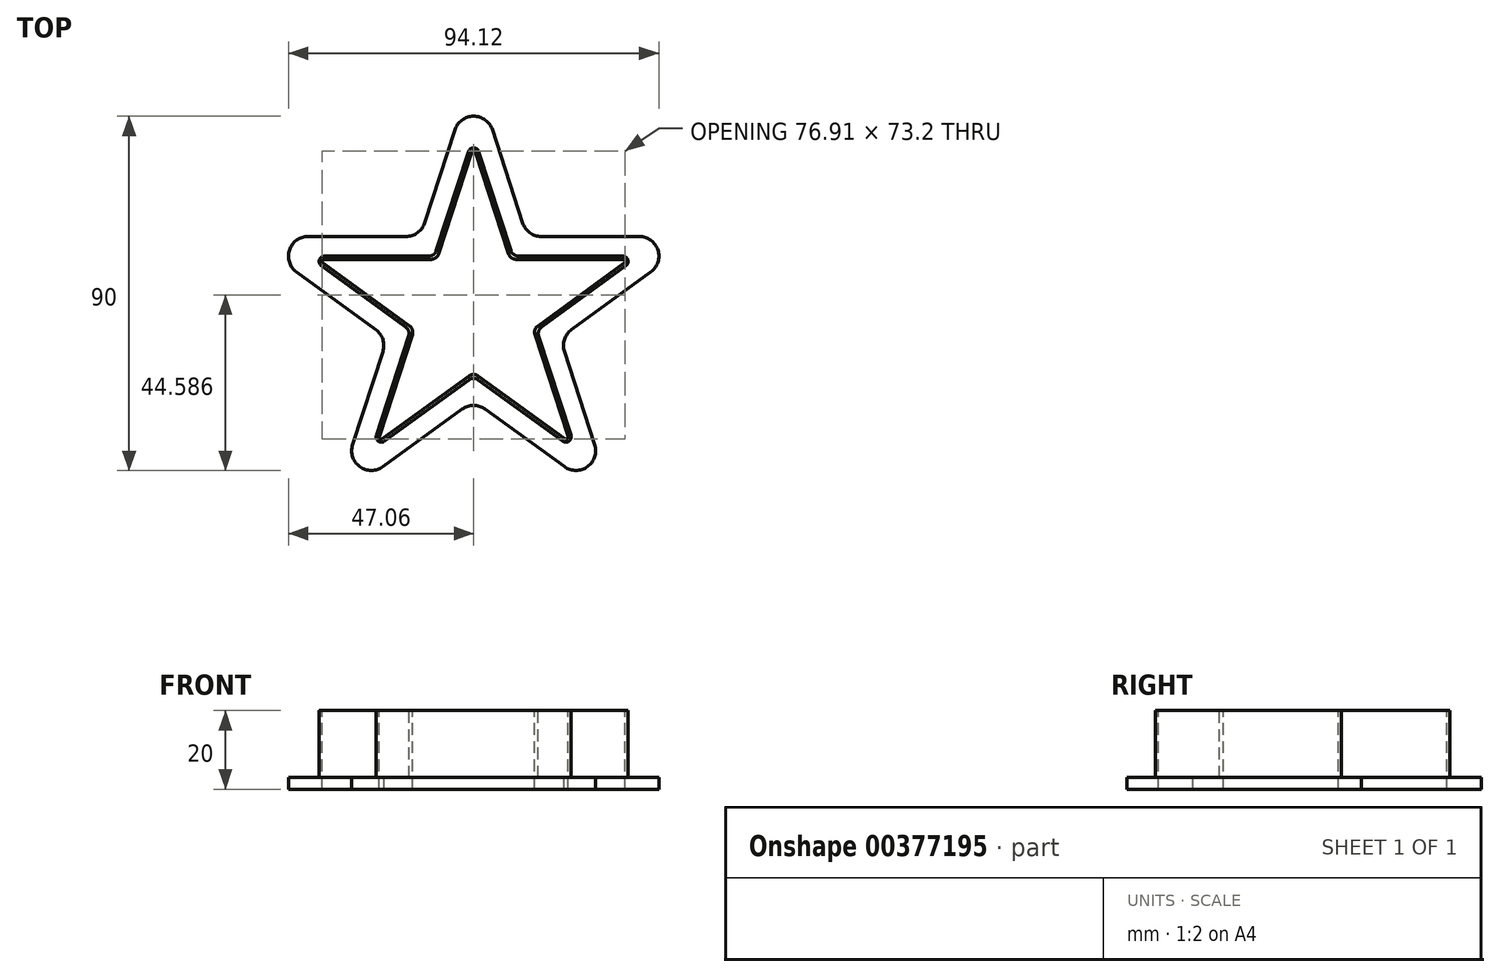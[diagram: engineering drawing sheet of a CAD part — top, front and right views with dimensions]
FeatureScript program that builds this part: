
annotation { "Feature Type Name" : "Feature", "Feature Type Description" : "" }
export const myFeature = defineFeature(function(context is Context, id is Id, definition is map)
    precondition{}
    {
        {
            var Q0;
            Q0=qCreatedBy(makeId("Top.planeOp"),FACE);
            var sketch = newSketch(context, id + "F0", { "sketchPlane" : qUnion([Q0])});
            skPoint(sketch, "E0.0.midPoint", {"position": v(8.03, -32.44) * mm});
            skPoint(sketch, "E1.endSnap0", {"position": v(0, -7.72) * mm});
            skLineSegment(sketch, "E2", {"start": v(-9.93, 13.67) * mm, "end": v(-1.28, 40.27) * mm});
            skLineSegment(sketch, "E3", {"start": v(1.28, 40.27) * mm, "end": v(9.93, 13.67) * mm});
            skLineSegment(sketch, "E4.1.0", {"start": v(-16.06, -5.22) * mm, "end": v(-38.7, 11.22) * mm});
            skLineSegment(sketch, "E4.1.1", {"start": v(-37.9, 13.67) * mm, "end": v(-9.93, 13.67) * mm});
            skLineSegment(sketch, "E4.2.0", {"start": v(0, -16.9) * mm, "end": v(-22.63, -33.33) * mm});
            skLineSegment(sketch, "E4.2.1", {"start": v(-24.7, -31.83) * mm, "end": v(-16.06, -5.22) * mm});
            skLineSegment(sketch, "E4.3.0", {"start": v(16.06, -5.22) * mm, "end": v(24.7, -31.83) * mm});
            skLineSegment(sketch, "E4.3.1", {"start": v(22.63, -33.33) * mm, "end": v(0, -16.9) * mm});
            skLineSegment(sketch, "E4.4.0", {"start": v(9.93, 13.67) * mm, "end": v(37.9, 13.67) * mm});
            skLineSegment(sketch, "E4.4.1", {"start": v(38.7, 11.22) * mm, "end": v(16.06, -5.22) * mm});
            skPoint(sketch, "E4.center", {"position": v(0, 0) * mm});
            skLineSegment(sketch, "E5.0", {"start": v(-57.45, 18.67) * mm, "end": v(-13.56, 18.67) * mm});
            skLineSegment(sketch, "E5.1", {"start": v(-21.94, -7.13) * mm, "end": v(-57.45, 18.67) * mm});
            skLineSegment(sketch, "E5.2", {"start": v(-13.56, 18.67) * mm, "end": v(0, 60.4) * mm});
            skLineSegment(sketch, "E5.3", {"start": v(-35.5, -48.87) * mm, "end": v(-21.94, -7.13) * mm});
            skLineSegment(sketch, "E5.4", {"start": v(0, -23.07) * mm, "end": v(-35.5, -48.87) * mm});
            skLineSegment(sketch, "E5.5", {"start": v(35.5, -48.87) * mm, "end": v(0, -23.07) * mm});
            skLineSegment(sketch, "E5.6", {"start": v(0, 60.4) * mm, "end": v(13.56, 18.67) * mm});
            skLineSegment(sketch, "E5.7", {"start": v(13.56, 18.67) * mm, "end": v(57.45, 18.67) * mm});
            skLineSegment(sketch, "E5.8", {"start": v(57.45, 18.67) * mm, "end": v(21.94, -7.13) * mm});
            skLineSegment(sketch, "E5.9", {"start": v(21.94, -7.13) * mm, "end": v(35.5, -48.87) * mm});
            skLineSegment(sketch, "E6.0", {"start": v(-15.12, -4.91) * mm, "end": v(-38.23, 11.87) * mm});
            skLineSegment(sketch, "E6.1", {"start": v(-23.95, -32.07) * mm, "end": v(-15.12, -4.91) * mm});
            skLineSegment(sketch, "E6.2", {"start": v(-37.9, 12.87) * mm, "end": v(-9.35, 12.87) * mm});
            skLineSegment(sketch, "E6.3", {"start": v(0, -15.9) * mm, "end": v(-23.1, -32.69) * mm});
            skLineSegment(sketch, "E6.4", {"start": v(23.1, -32.69) * mm, "end": v(0, -15.9) * mm});
            skLineSegment(sketch, "E6.5", {"start": v(15.12, -4.91) * mm, "end": v(23.95, -32.07) * mm});
            skLineSegment(sketch, "E6.6", {"start": v(-9.35, 12.87) * mm, "end": v(-0.52, 40.02) * mm});
            skLineSegment(sketch, "E6.7", {"start": v(0.52, 40.02) * mm, "end": v(9.35, 12.87) * mm});
            skLineSegment(sketch, "E6.8", {"start": v(9.35, 12.87) * mm, "end": v(37.9, 12.87) * mm});
            skLineSegment(sketch, "E6.9", {"start": v(38.23, 11.87) * mm, "end": v(15.12, -4.91) * mm});
            skPoint(sketch, "E7.visualSharp", {"position": v(39.6, 12.87) * mm});
            skArc(sketch, "E7.filletArc", {"start": v(38.23, 11.87) * mm, "mid": v(38.43, 12.49) * mm, "end": v(37.9, 12.87) * mm});
            skPoint(sketch, "E8.visualSharp", {"position": v(42.06, 13.67) * mm});
            skArc(sketch, "E8.filletArc", {"start": v(38.7, 11.22) * mm, "mid": v(39.19, 12.73) * mm, "end": v(37.9, 13.67) * mm});
            skPoint(sketch, "E9.visualSharp", {"position": v(0, 41.63) * mm});
            skArc(sketch, "E9.filletArc", {"start": v(0.52, 40.02) * mm, "mid": v(0, 40.4) * mm, "end": v(-0.52, 40.02) * mm});
            skPoint(sketch, "E10.visualSharp", {"position": v(-39.6, 12.87) * mm});
            skArc(sketch, "E10.filletArc", {"start": v(-37.9, 12.87) * mm, "mid": v(-38.43, 12.49) * mm, "end": v(-38.23, 11.87) * mm});
            skPoint(sketch, "E11.visualSharp", {"position": v(-24.47, -33.68) * mm});
            skArc(sketch, "E11.filletArc", {"start": v(-23.95, -32.07) * mm, "mid": v(-23.75, -32.69) * mm, "end": v(-23.1, -32.69) * mm});
            skPoint(sketch, "E12.visualSharp", {"position": v(24.47, -33.68) * mm});
            skArc(sketch, "E12.filletArc", {"start": v(23.1, -32.69) * mm, "mid": v(23.75, -32.69) * mm, "end": v(23.95, -32.07) * mm});
            skPoint(sketch, "E13.visualSharp", {"position": v(0, 44.22) * mm});
            skArc(sketch, "E13.filletArc", {"start": v(1.28, 40.27) * mm, "mid": v(0, 41.2) * mm, "end": v(-1.28, 40.27) * mm});
            skPoint(sketch, "E14.visualSharp", {"position": v(-42.06, 13.67) * mm});
            skArc(sketch, "E14.filletArc", {"start": v(-37.9, 13.67) * mm, "mid": v(-39.19, 12.73) * mm, "end": v(-38.7, 11.22) * mm});
            skPoint(sketch, "E15.visualSharp", {"position": v(-26, -35.78) * mm});
            skArc(sketch, "E15.filletArc", {"start": v(-24.7, -31.83) * mm, "mid": v(-24.22, -33.33) * mm, "end": v(-22.63, -33.33) * mm});
            skPoint(sketch, "E16.visualSharp", {"position": v(26, -35.78) * mm});
            skArc(sketch, "E16.filletArc", {"start": v(22.63, -33.33) * mm, "mid": v(24.22, -33.33) * mm, "end": v(24.7, -31.83) * mm});
            skSolve(sketch);
        }
        {
            var Q0;
            Q0=makeQuery(id+"F0.imprint","IMPRINT",FACE,{"disambiguationData":[TD([[makeQuery(id+"F0.imprint","IMPRINT",EDGE,{"derivedFrom":sQuery(id+"F0.wireOp",EDGE,"E2")}),1.0]])]});
            var Q1;
            Q1=makeQuery(id+"F0.imprint","IMPRINT",FACE,{"disambiguationData":[TD([[makeQuery(id+"F0.imprint","IMPRINT",EDGE,{"derivedFrom":sQuery(id+"F0.wireOp",EDGE,"E2")}),-1.0]])]});
            extrude(context, id + "F1", {"entities" : qUnion([Q0, Q1]), "oppositeDirection" : true, "depth" : 3 * mm});
        }
        {
            var Q0;
            Q0=makeQuery(id+"F0.imprint","IMPRINT",FACE,{"disambiguationData":[TD([[makeQuery(id+"F0.imprint","IMPRINT",EDGE,{"derivedFrom":sQuery(id+"F0.wireOp",EDGE,"E2")}),-1.0]])]});
            extrude(context, id + "F2", {"entities" : qUnion([Q0]), "operationType" : NewBodyOperationType.ADD, "depth" : 17 * mm});
        }
        {
            var Q0;
            Q0=makeQuery(id+"F1.opExtrude","SWEPT_EDGE",EDGE,{"disambiguationData":[OSD([sQuery(id+"F0.wireOp",EDGE,"E5.3"),sQuery(id+"F0.wireOp",EDGE,"E5.4")])]});
            var Q1;
            Q1=makeQuery(id+"F1.opExtrude","SWEPT_EDGE",EDGE,{"disambiguationData":[OSD([sQuery(id+"F0.wireOp",EDGE,"E5.0"),sQuery(id+"F0.wireOp",EDGE,"E5.1")])]});
            var Q2;
            Q2=makeQuery(id+"F1.opExtrude","SWEPT_EDGE",EDGE,{"disambiguationData":[OSD([sQuery(id+"F0.wireOp",EDGE,"E5.5"),sQuery(id+"F0.wireOp",EDGE,"E5.9")])]});
            var Q3;
            Q3=makeQuery(id+"F1.opExtrude","SWEPT_EDGE",EDGE,{"disambiguationData":[OSD([sQuery(id+"F0.wireOp",EDGE,"E5.2"),sQuery(id+"F0.wireOp",EDGE,"E5.6")])]});
            var Q4;
            Q4=makeQuery(id+"F1.opExtrude","SWEPT_EDGE",EDGE,{"disambiguationData":[OSD([sQuery(id+"F0.wireOp",EDGE,"E5.7"),sQuery(id+"F0.wireOp",EDGE,"E5.8")])]});
            fillet(context, id + "F3", {"entities" : qUnion([Q0, Q1, Q2, Q3, Q4]), "radius" : 5 * mm, "tangentPropagation" : true, "allowEdgeOverflow" : false});
        }
        {
            var Q0;
            Q0=makeQuery(id+"F1.opExtrude","SWEPT_EDGE",EDGE,{"disambiguationData":[OSD([sQuery(id+"F0.wireOp",EDGE,"E5.1"),sQuery(id+"F0.wireOp",EDGE,"E5.3")])]});
            var Q1;
            Q1=makeQuery(id+"F1.opExtrude","SWEPT_EDGE",EDGE,{"disambiguationData":[OSD([sQuery(id+"F0.wireOp",EDGE,"E5.0"),sQuery(id+"F0.wireOp",EDGE,"E5.2")])]});
            var Q2;
            Q2=makeQuery(id+"F1.opExtrude","SWEPT_EDGE",EDGE,{"disambiguationData":[OSD([sQuery(id+"F0.wireOp",EDGE,"E5.6"),sQuery(id+"F0.wireOp",EDGE,"E5.7")])]});
            var Q3;
            Q3=makeQuery(id+"F1.opExtrude","SWEPT_EDGE",EDGE,{"disambiguationData":[OSD([sQuery(id+"F0.wireOp",EDGE,"E5.8"),sQuery(id+"F0.wireOp",EDGE,"E5.9")])]});
            var Q4;
            Q4=makeQuery(id+"F1.opExtrude","SWEPT_EDGE",EDGE,{"disambiguationData":[OSD([sQuery(id+"F0.wireOp",EDGE,"E5.4"),sQuery(id+"F0.wireOp",EDGE,"E5.5")])]});
            fillet(context, id + "F4", {"entities" : qUnion([Q0, Q1, Q2, Q3, Q4]), "radius" : 5 * mm, "tangentPropagation" : true, "allowEdgeOverflow" : false});
        }
        {
            var Q0;
            {var subQ0=sQuery(id+"F0.wireOp",EDGE,"E6.6");var subQ1=sQuery(id+"F0.wireOp",EDGE,"E6.2");Q0=makeQuery(id+"F2.boolean.opBoolean","MERGE",EDGE,{"derivedFrom":[makeQuery(id+"F1.opExtrude","SWEPT_EDGE",EDGE,{"disambiguationData":[OSD([subQ1,subQ0])]}),makeQuery(id+"F2.opExtrude","SWEPT_EDGE",EDGE,{"disambiguationData":[OSD([subQ1,subQ0])]})]});}
            var Q1;
            Q1=makeQuery(id+"F2.opExtrude","SWEPT_EDGE",EDGE,{"disambiguationData":[OSD([sQuery(id+"F0.wireOp",EDGE,"E2"),sQuery(id+"F0.wireOp",EDGE,"E4.1.1")])]});
            var Q2;
            Q2=makeQuery(id+"F2.opExtrude","SWEPT_EDGE",EDGE,{"disambiguationData":[OSD([sQuery(id+"F0.wireOp",EDGE,"E3"),sQuery(id+"F0.wireOp",EDGE,"E4.4.0")])]});
            var Q3;
            {var subQ0=sQuery(id+"F0.wireOp",EDGE,"E6.8");var subQ1=sQuery(id+"F0.wireOp",EDGE,"E6.7");Q3=makeQuery(id+"F2.boolean.opBoolean","MERGE",EDGE,{"derivedFrom":[makeQuery(id+"F1.opExtrude","SWEPT_EDGE",EDGE,{"disambiguationData":[OSD([subQ1,subQ0])]}),makeQuery(id+"F2.opExtrude","SWEPT_EDGE",EDGE,{"disambiguationData":[OSD([subQ1,subQ0])]})]});}
            var Q4;
            Q4=makeQuery(id+"F2.opExtrude","SWEPT_EDGE",EDGE,{"disambiguationData":[OSD([sQuery(id+"F0.wireOp",EDGE,"E4.3.0"),sQuery(id+"F0.wireOp",EDGE,"E4.4.1")])]});
            var Q5;
            {var subQ0=sQuery(id+"F0.wireOp",EDGE,"E6.9");var subQ1=sQuery(id+"F0.wireOp",EDGE,"E6.5");Q5=makeQuery(id+"F2.boolean.opBoolean","MERGE",EDGE,{"derivedFrom":[makeQuery(id+"F1.opExtrude","SWEPT_EDGE",EDGE,{"disambiguationData":[OSD([subQ1,subQ0])]}),makeQuery(id+"F2.opExtrude","SWEPT_EDGE",EDGE,{"disambiguationData":[OSD([subQ1,subQ0])]})]});}
            var Q6;
            {var subQ0=sQuery(id+"F0.wireOp",EDGE,"E6.1");var subQ1=sQuery(id+"F0.wireOp",EDGE,"E6.0");Q6=makeQuery(id+"F2.boolean.opBoolean","MERGE",EDGE,{"derivedFrom":[makeQuery(id+"F1.opExtrude","SWEPT_EDGE",EDGE,{"disambiguationData":[OSD([subQ1,subQ0])]}),makeQuery(id+"F2.opExtrude","SWEPT_EDGE",EDGE,{"disambiguationData":[OSD([subQ1,subQ0])]})]});}
            var Q7;
            Q7=makeQuery(id+"F2.opExtrude","SWEPT_EDGE",EDGE,{"disambiguationData":[OSD([sQuery(id+"F0.wireOp",EDGE,"E4.1.0"),sQuery(id+"F0.wireOp",EDGE,"E4.2.1")])]});
            var Q8;
            {var subQ0=sQuery(id+"F0.wireOp",EDGE,"E6.4");var subQ1=sQuery(id+"F0.wireOp",EDGE,"E6.3");Q8=makeQuery(id+"F2.boolean.opBoolean","MERGE",EDGE,{"derivedFrom":[makeQuery(id+"F1.opExtrude","SWEPT_EDGE",EDGE,{"disambiguationData":[OSD([subQ1,subQ0])]}),makeQuery(id+"F2.opExtrude","SWEPT_EDGE",EDGE,{"disambiguationData":[OSD([subQ1,subQ0])]})]});}
            var Q9;
            Q9=makeQuery(id+"F2.opExtrude","SWEPT_EDGE",EDGE,{"disambiguationData":[OSD([sQuery(id+"F0.wireOp",EDGE,"E4.2.0"),sQuery(id+"F0.wireOp",EDGE,"E4.3.1")])]});
            fillet(context, id + "F5", {"entities" : qUnion([Q0, Q1, Q2, Q3, Q4, Q5, Q6, Q7, Q8, Q9]), "radius" : 2 * mm, "tangentPropagation" : true, "allowEdgeOverflow" : false});
        }
    });
